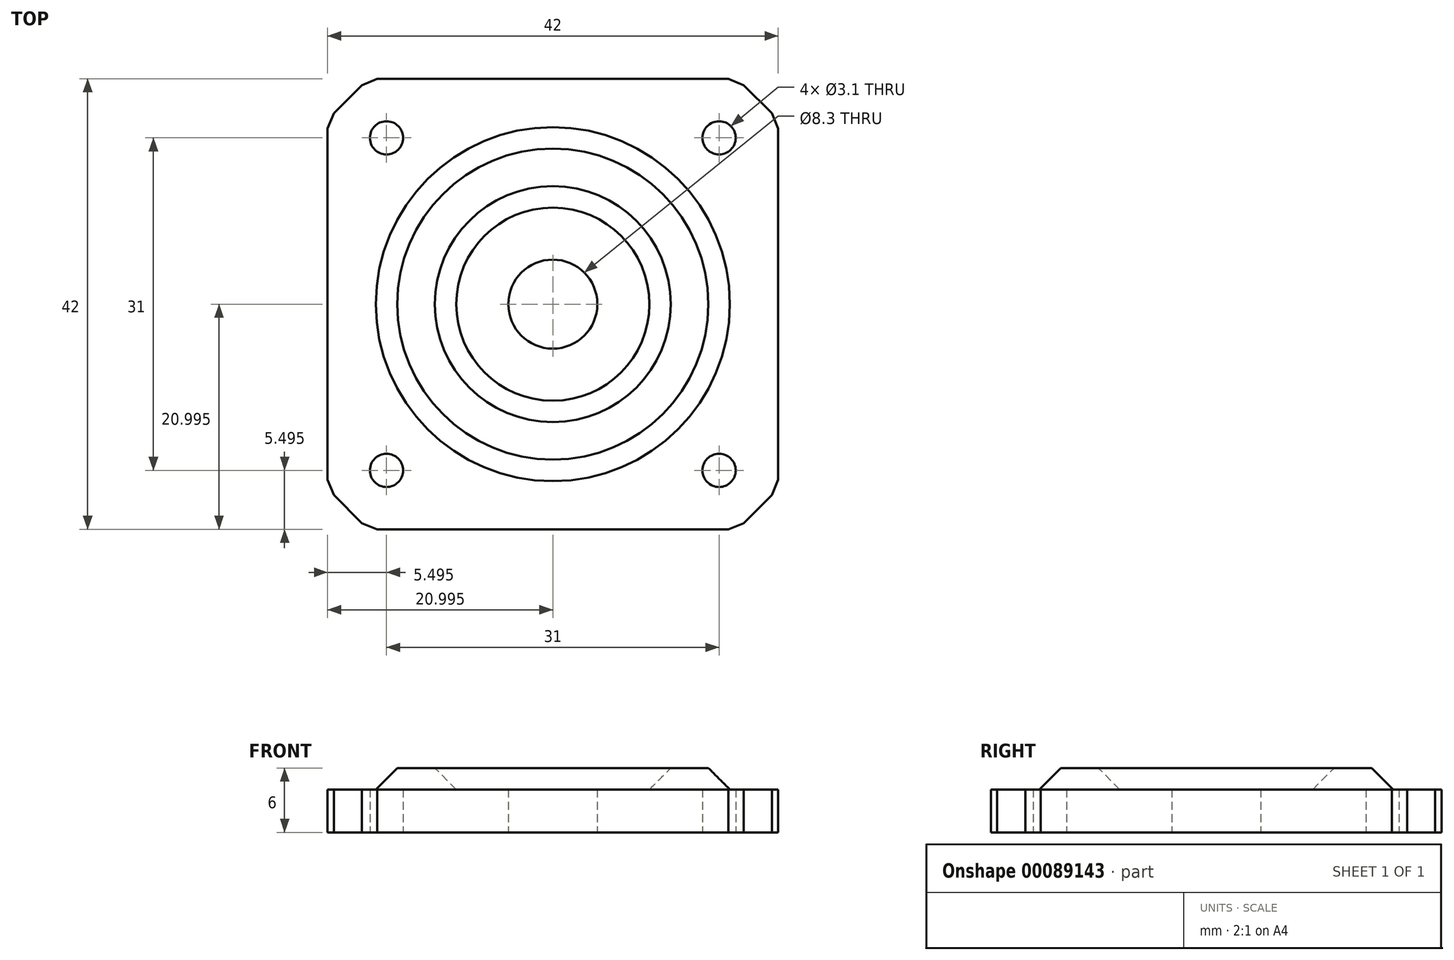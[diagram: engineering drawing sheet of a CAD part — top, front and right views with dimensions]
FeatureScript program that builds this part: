
annotation { "Feature Type Name" : "Feature", "Feature Type Description" : "" }
export const myFeature = defineFeature(function(context is Context, id is Id, definition is map)
    precondition{}
    {
        {
            var Q0;
            Q0=qCreatedBy(makeId("Top.planeOp"),FACE);
            var sketch = newSketch(context, id + "F0", { "sketchPlane" : qUnion([Q0])});
            skLineSegment(sketch, "E0.bottom", {"start": v(-45.1, 45.1) * mm, "end": v(45.1, 45.1) * mm});
            skLineSegment(sketch, "E0.top", {"start": v(-45.1, -45.1) * mm, "end": v(45.1, -45.1) * mm});
            skLineSegment(sketch, "E0.left", {"start": v(-45.1, 45.1) * mm, "end": v(-45.1, -45.1) * mm});
            skLineSegment(sketch, "E0.right", {"start": v(45.1, 45.1) * mm, "end": v(45.1, -45.1) * mm});
            skFitSpline(sketch, "E1.0", {"points": [v(15.6, 14.68) * mm, v(15.6, 3.76) * mm, v(15.6, -7.15) * mm, v(15.6, -18.07) * mm], "construction": true});
            skFitSpline(sketch, "E1.1", {"points": [v(15.02, -19.48) * mm, v(15.2, -19.3) * mm, v(15.35, -19.08) * mm, v(15.45, -18.83) * mm, v(15.5, -18.7) * mm, v(15.54, -18.58) * mm, v(15.57, -18.45) * mm, v(15.6, -18.33) * mm, v(15.6, -18.2) * mm, v(15.6, -18.07) * mm], "construction": true});
            skFitSpline(sketch, "E1.2", {"points": [v(15.02, -19.48) * mm, v(14.14, -20.36) * mm, v(13.27, -21.23) * mm, v(12.4, -22.1) * mm], "construction": true});
            skFitSpline(sketch, "E1.3", {"points": [v(10.98, -22.7) * mm, v(11.24, -22.7) * mm, v(11.5, -22.64) * mm, v(11.74, -22.54) * mm, v(11.86, -22.5) * mm, v(11.98, -22.43) * mm, v(12.1, -22.36) * mm, v(12.2, -22.28) * mm, v(12.3, -22.2) * mm, v(12.4, -22.1) * mm], "construction": true});
            skFitSpline(sketch, "E1.5", {"points": [v(15.6, 14.68) * mm, v(15.6, 14.94) * mm, v(15.55, 15.2) * mm, v(15.45, 15.44) * mm, v(15.4, 15.56) * mm, v(15.34, 15.68) * mm, v(15.27, 15.8) * mm, v(15.2, 15.9) * mm, v(15.11, 16) * mm, v(15.02, 16.1) * mm], "construction": true});
            skFitSpline(sketch, "E1.6", {"points": [v(12.4, 18.72) * mm, v(13.27, 17.84) * mm, v(14.14, 16.97) * mm, v(15.02, 16.1) * mm], "construction": true});
            skFitSpline(sketch, "E1.7", {"points": [v(12.4, 18.72) * mm, v(12.2, 18.9) * mm, v(11.99, 19.05) * mm, v(11.74, 19.15) * mm, v(11.62, 19.2) * mm, v(11.5, 19.24) * mm, v(11.36, 19.27) * mm, v(11.24, 19.3) * mm, v(11.1, 19.3) * mm, v(10.98, 19.3) * mm], "construction": true});
            skFitSpline(sketch, "E1.8", {"points": [v(-21.77, 19.3) * mm, v(-10.85, 19.3) * mm, v(0.06, 19.3) * mm, v(10.98, 19.3) * mm], "construction": true});
            skFitSpline(sketch, "E1.9", {"points": [v(10.1, 15.36) * mm, v(10.31, 15.36) * mm, v(10.5, 15.32) * mm, v(10.7, 15.24) * mm, v(10.89, 15.16) * mm, v(11.06, 15.05) * mm, v(11.2, 14.9) * mm, v(11.35, 14.76) * mm, v(11.46, 14.59) * mm, v(11.54, 14.4) * mm, v(11.62, 14.2) * mm, v(11.66, 14.01) * mm, v(11.66, 13.8) * mm, v(11.66, 13.6) * mm, v(11.62, 13.4) * mm, v(11.54, 13.21) * mm, v(11.46, 13.02) * mm, v(11.35, 12.86) * mm, v(11.2, 12.7) * mm, v(11.06, 12.56) * mm, v(10.89, 12.45) * mm, v(10.7, 12.37) * mm, v(10.5, 12.3) * mm, v(10.31, 12.26) * mm, v(10.1, 12.26) * mm], "construction": true});
            skFitSpline(sketch, "E1.10", {"points": [v(10.1, 12.26) * mm, v(9.9, 12.26) * mm, v(9.7, 12.3) * mm, v(9.51, 12.37) * mm, v(9.32, 12.45) * mm, v(9.16, 12.56) * mm, v(9, 12.7) * mm, v(8.86, 12.85) * mm, v(8.75, 13.02) * mm, v(8.67, 13.21) * mm, v(8.6, 13.4) * mm, v(8.56, 13.6) * mm, v(8.56, 13.8) * mm, v(8.56, 14.01) * mm, v(8.6, 14.2) * mm, v(8.67, 14.4) * mm, v(8.75, 14.59) * mm, v(8.86, 14.76) * mm, v(9, 14.9) * mm, v(9.15, 15.05) * mm, v(9.32, 15.16) * mm, v(9.51, 15.24) * mm, v(9.7, 15.32) * mm, v(9.9, 15.36) * mm, v(10.1, 15.36) * mm], "construction": true});
            skFitSpline(sketch, "E1.11", {"points": [v(-5.4, 14.8) * mm, v(-4.31, 14.8) * mm, v(-3.24, 14.7) * mm, v(-2.18, 14.49) * mm, v(-1.11, 14.28) * mm, v(-0.08, 13.96) * mm, v(0.92, 13.55) * mm, v(1.92, 13.14) * mm, v(2.87, 12.63) * mm, v(3.77, 12.02) * mm, v(4.67, 11.42) * mm, v(5.5, 10.74) * mm, v(6.27, 9.97) * mm, v(7.04, 9.2) * mm, v(7.72, 8.37) * mm, v(8.32, 7.47) * mm, v(8.93, 6.57) * mm, v(9.43, 5.62) * mm, v(9.85, 4.62) * mm, v(10.26, 3.62) * mm, v(10.58, 2.59) * mm, v(10.79, 1.52) * mm, v(11, 0.46) * mm, v(11.1, -0.61) * mm, v(11.1, -1.7) * mm, v(11.1, -2.78) * mm, v(11, -3.85) * mm, v(10.79, -4.91) * mm, v(10.58, -5.98) * mm, v(10.26, -7) * mm, v(9.85, -8) * mm, v(9.44, -9) * mm, v(8.93, -9.96) * mm, v(8.32, -10.86) * mm, v(7.72, -11.76) * mm, v(7.04, -12.6) * mm, v(6.27, -13.36) * mm, v(5.5, -14.13) * mm, v(4.67, -14.81) * mm, v(3.77, -15.41) * mm, v(2.87, -16.02) * mm, v(1.92, -16.52) * mm, v(0.92, -16.94) * mm, v(-0.08, -17.35) * mm, v(-1.11, -17.67) * mm, v(-2.18, -17.88) * mm, v(-3.24, -18.09) * mm, v(-4.31, -18.2) * mm, v(-5.4, -18.2) * mm], "construction": true});
            skFitSpline(sketch, "E1.12", {"points": [v(-5.4, -12.7) * mm, v(-4.9, -12.7) * mm, v(-4.42, -12.66) * mm, v(-3.93, -12.6) * mm, v(-3.39, -12.52) * mm, v(-2.85, -12.4) * mm, v(-2.31, -12.25) * mm, v(-1.72, -12.08) * mm, v(-1.14, -11.86) * mm, v(-0.57, -11.58) * mm, v(0.05, -11.28) * mm, v(0.65, -10.91) * mm, v(1.2, -10.5) * mm, v(1.82, -10.03) * mm, v(2.39, -9.5) * mm, v(2.9, -8.93) * mm, v(3.44, -8.3) * mm, v(3.92, -7.61) * mm, v(4.31, -6.87) * mm, v(4.73, -6.09) * mm, v(5.05, -5.26) * mm, v(5.27, -4.4) * mm, v(5.5, -3.51) * mm, v(5.6, -2.61) * mm, v(5.6, -1.7) * mm, v(5.6, -0.78) * mm, v(5.5, 0.12) * mm, v(5.27, 1.01) * mm, v(5.05, 1.87) * mm, v(4.73, 2.7) * mm, v(4.31, 3.48) * mm, v(3.92, 4.22) * mm, v(3.44, 4.9) * mm, v(2.9, 5.54) * mm, v(2.39, 6.12) * mm, v(1.82, 6.64) * mm, v(1.2, 7.1) * mm, v(0.65, 7.52) * mm, v(0.05, 7.89) * mm, v(-0.57, 8.2) * mm, v(-1.13, 8.47) * mm, v(-1.72, 8.7) * mm, v(-2.31, 8.87) * mm, v(-2.85, 9.02) * mm, v(-3.39, 9.13) * mm, v(-3.93, 9.2) * mm, v(-4.42, 9.27) * mm, v(-4.9, 9.3) * mm, v(-5.4, 9.3) * mm], "construction": true});
            skFitSpline(sketch, "E1.13", {"points": [v(-5.4, 2.46) * mm, v(-5, 2.46) * mm, v(-4.61, 2.4) * mm, v(-4.23, 2.29) * mm, v(-3.75, 2.15) * mm, v(-3.3, 1.93) * mm, v(-2.9, 1.63) * mm, v(-2.67, 1.45) * mm, v(-2.46, 1.25) * mm, v(-2.27, 1.03) * mm, v(-2.06, 0.8) * mm, v(-1.88, 0.54) * mm, v(-1.73, 0.26) * mm, v(-1.58, -0.04) * mm, v(-1.46, -0.35) * mm, v(-1.37, -0.67) * mm, v(-1.29, -1) * mm, v(-1.24, -1.35) * mm, v(-1.24, -1.7) * mm, v(-1.24, -2.04) * mm, v(-1.29, -2.38) * mm, v(-1.37, -2.72) * mm, v(-1.45, -3.04) * mm, v(-1.57, -3.35) * mm, v(-1.73, -3.65) * mm, v(-1.88, -3.93) * mm, v(-2.06, -4.18) * mm, v(-2.27, -4.42) * mm, v(-2.46, -4.64) * mm, v(-2.67, -4.84) * mm, v(-2.9, -5.01) * mm, v(-3.3, -5.32) * mm, v(-3.75, -5.54) * mm, v(-4.23, -5.68) * mm, v(-4.61, -5.79) * mm, v(-5, -5.84) * mm, v(-5.4, -5.84) * mm], "construction": true});
            skLineSegment(sketch, "E2", {"start": v(-5.4, 19.3) * mm, "end": v(10.98, 19.3) * mm});
            skLineSegment(sketch, "E3", {"start": v(12.4, 18.72) * mm, "end": v(15.02, 16.1) * mm});
            skLineSegment(sketch, "E4", {"start": v(15.6, 14.68) * mm, "end": v(15.6, -18.07) * mm});
            skLineSegment(sketch, "E5", {"start": v(15.02, -19.48) * mm, "end": v(12.4, -22.1) * mm});
            skLineSegment(sketch, "E6", {"start": v(10.98, -22.7) * mm, "end": v(-5.4, -22.7) * mm});
            skLineSegment(sketch, "E7", {"start": v(10.1, -15.64) * mm, "end": v(10.1, -18.74) * mm, "construction": true});
            skCircle(sketch, "E8", {"center": v(10.1, -17.2) * mm, "radius": 1.55 * mm});
            skLineSegment(sketch, "E9", {"start": v(10.1, 15.36) * mm, "end": v(10.1, 12.26) * mm, "construction": true});
            skCircle(sketch, "E10", {"center": v(10.1, 13.8) * mm, "radius": 1.55 * mm});
            skCircle(sketch, "E11", {"center": v(-5.4, -1.7) * mm, "radius": 16.5 * mm});
            skCircle(sketch, "E12", {"center": v(-5.4, -1.7) * mm, "radius": 11 * mm});
            skCircle(sketch, "E13", {"center": v(-5.4, -1.7) * mm, "radius": 4.15 * mm});
            skLineSegment(sketch, "E14", {"start": v(15.02, 16.1) * mm, "end": v(15.6, 14.68) * mm});
            skLineSegment(sketch, "E15", {"start": v(10.98, 19.3) * mm, "end": v(12.4, 18.72) * mm});
            skLineSegment(sketch, "E16", {"start": v(15.6, -18.07) * mm, "end": v(15.02, -19.48) * mm});
            skLineSegment(sketch, "E17", {"start": v(12.4, -22.1) * mm, "end": v(10.98, -22.7) * mm});
            skLineSegment(sketch, "E18.MirrorCS", {"start": v(-5.4, 19.3) * mm, "end": v(-21.77, 19.3) * mm});
            skLineSegment(sketch, "E19.MirrorCS", {"start": v(-21.77, 19.3) * mm, "end": v(-23.18, 18.72) * mm});
            skLineSegment(sketch, "E20.MirrorCS", {"start": v(-23.18, 18.72) * mm, "end": v(-25.8, 16.1) * mm});
            skLineSegment(sketch, "E21.MirrorCS", {"start": v(-25.8, 16.1) * mm, "end": v(-26.4, 14.68) * mm});
            skLineSegment(sketch, "E22.MirrorCS", {"start": v(-26.4, 14.68) * mm, "end": v(-26.4, -18.07) * mm});
            skLineSegment(sketch, "E23.MirrorCS", {"start": v(-26.4, -18.07) * mm, "end": v(-25.8, -19.48) * mm});
            skLineSegment(sketch, "E24.MirrorCS", {"start": v(-25.8, -19.48) * mm, "end": v(-23.18, -22.1) * mm});
            skLineSegment(sketch, "E25.MirrorCS", {"start": v(-23.18, -22.1) * mm, "end": v(-21.77, -22.7) * mm});
            skLineSegment(sketch, "E26.MirrorCS", {"start": v(-21.77, -22.7) * mm, "end": v(-5.4, -22.7) * mm});
            skCircle(sketch, "E27.MirrorC", {"center": v(-20.9, -17.2) * mm, "radius": 1.55 * mm});
            skCircle(sketch, "E28.MirrorC", {"center": v(-20.9, 13.8) * mm, "radius": 1.55 * mm});
            skSolve(sketch);
        }
        {
            var Q0;
            Q0=makeQuery(id+"F0.imprint","IMPRINT",FACE,{"disambiguationData":[TD([[makeQuery(id+"F0.imprint","IMPRINT",EDGE,{"derivedFrom":sQuery(id+"F0.wireOp",EDGE,"E2")}),-1.0]])]});
            var Q1;
            Q1=makeQuery(id+"F0.imprint","IMPRINT",FACE,{"disambiguationData":[TD([[makeQuery(id+"F0.imprint","IMPRINT",EDGE,{"derivedFrom":sQuery(id+"F0.wireOp",EDGE,"E11")}),1.0]])]});
            var Q2;
            Q2=makeQuery(id+"F0.imprint","IMPRINT",FACE,{"disambiguationData":[TD([[makeQuery(id+"F0.imprint","IMPRINT",EDGE,{"derivedFrom":sQuery(id+"F0.wireOp",EDGE,"E12")}),1.0]])]});
            extrude(context, id + "F1", {"entities" : qUnion([Q0, Q1, Q2]), "depth" : 4 * mm});
        }
        {
            var Q0;
            Q0=makeQuery(id+"F1.opExtrude","CAP_FACE",FACE,{"disambiguationData":[OSD([sQuery(id+"F0.wireOp",EDGE,"E2"),sQuery(id+"F0.wireOp",EDGE,"E3"),sQuery(id+"F0.wireOp",EDGE,"E4"),sQuery(id+"F0.wireOp",EDGE,"E5"),sQuery(id+"F0.wireOp",EDGE,"E6"),sQuery(id+"F0.wireOp",EDGE,"E8"),sQuery(id+"F0.wireOp",EDGE,"E10"),sQuery(id+"F0.wireOp",EDGE,"E13"),sQuery(id+"F0.wireOp",EDGE,"E14"),sQuery(id+"F0.wireOp",EDGE,"E15"),sQuery(id+"F0.wireOp",EDGE,"E16"),sQuery(id+"F0.wireOp",EDGE,"E17"),sQuery(id+"F0.wireOp",EDGE,"E18.MirrorCS"),sQuery(id+"F0.wireOp",EDGE,"E19.MirrorCS"),sQuery(id+"F0.wireOp",EDGE,"E20.MirrorCS"),sQuery(id+"F0.wireOp",EDGE,"E21.MirrorCS"),sQuery(id+"F0.wireOp",EDGE,"E22.MirrorCS"),sQuery(id+"F0.wireOp",EDGE,"E23.MirrorCS"),sQuery(id+"F0.wireOp",EDGE,"E24.MirrorCS"),sQuery(id+"F0.wireOp",EDGE,"E25.MirrorCS"),sQuery(id+"F0.wireOp",EDGE,"E26.MirrorCS"),sQuery(id+"F0.wireOp",EDGE,"E27.MirrorC"),sQuery(id+"F0.wireOp",EDGE,"E28.MirrorC")])],"isStart":false});
            var sketch = newSketch(context, id + "F2", { "sketchPlane" : qUnion([Q0])});
            skCircle(sketch, "E29.0", {"center": v(-5.4, -1.7) * mm, "radius": 11 * mm});
            skCircle(sketch, "E29.1", {"center": v(-5.4, -1.7) * mm, "radius": 16.5 * mm});
            skSolve(sketch);
        }
        {
            var Q0;
            Q0=makeQuery(id+"F2.imprint","IMPRINT",FACE,{"disambiguationData":[TD([[makeQuery(id+"F2.imprint","IMPRINT",EDGE,{"derivedFrom":sQuery(id+"F2.wireOp",EDGE,"E29.0")}),-1.0]])]});
            extrude(context, id + "F3", {"entities" : qUnion([Q0]), "operationType" : NewBodyOperationType.ADD, "depth" : 2 * mm});
        }
        {
            var Q0;
            Q0=makeQuery(id+"F3.opExtrude","CAP_EDGE",EDGE,{"disambiguationData":[OSD([sQuery(id+"F2.wireOp",EDGE,"E29.1")])],"isStart":false});
            chamfer(context, id + "F4", {"entities" : qUnion([Q0]), "width" : 2 * mm, "tangentPropagation" : true});
        }
        {
            var Q0;
            Q0=makeQuery(id+"F3.opExtrude","CAP_EDGE",EDGE,{"disambiguationData":[OSD([sQuery(id+"F2.wireOp",EDGE,"E29.0")])],"isStart":true});
            chamfer(context, id + "F5", {"entities" : qUnion([Q0]), "width" : 2 * mm, "tangentPropagation" : true});
        }
    });
